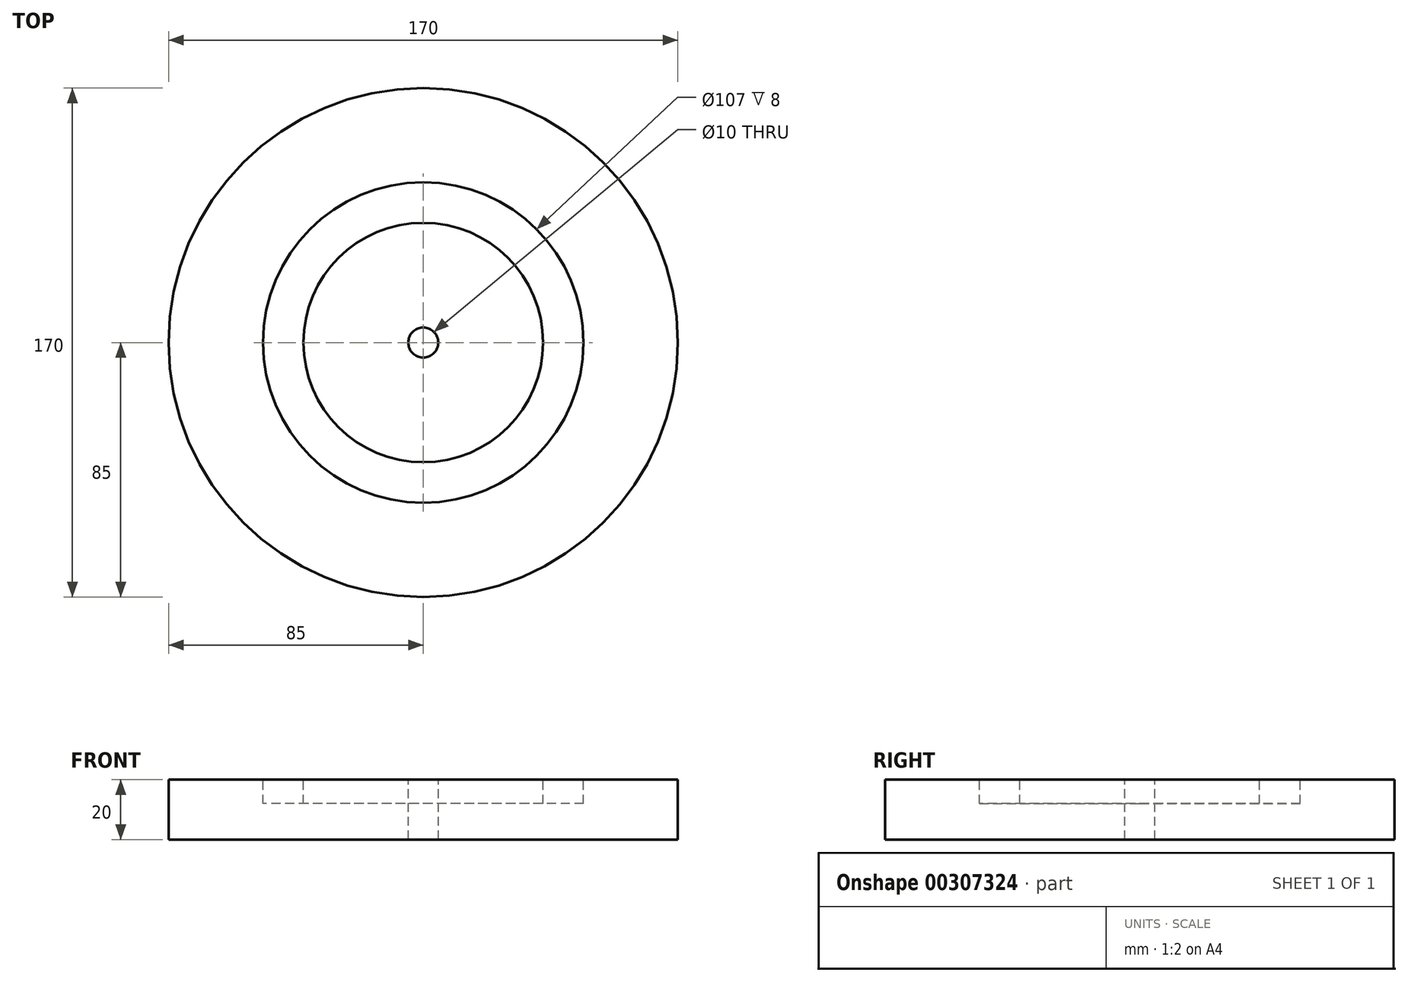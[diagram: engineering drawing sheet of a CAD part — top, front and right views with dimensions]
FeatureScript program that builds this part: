
annotation { "Feature Type Name" : "Feature", "Feature Type Description" : "" }
export const myFeature = defineFeature(function(context is Context, id is Id, definition is map)
    precondition{}
    {
        {
            var Q0;
            Q0=qCreatedBy(makeId("Top.planeOp"),FACE);
            var sketch = newSketch(context, id + "F0", { "sketchPlane" : qUnion([Q0])});
            skCircle(sketch, "E0", {"center": v(0, 0) * mm, "radius": 85 * mm});
            skSolve(sketch);
        }
        {
            var Q0;
            Q0=makeQuery(id+"F0.imprint","IMPRINT",FACE,{"disambiguationData":[TD([[makeQuery(id+"F0.imprint","IMPRINT",EDGE,{"derivedFrom":sQuery(id+"F0.wireOp",EDGE,"E0")}),1.0]])]});
            extrude(context, id + "F1", {"entities" : qUnion([Q0]), "depth" : 20 * mm});
        }
        {
            var Q0;
            Q0=makeQuery(id+"F1.opExtrude","CAP_FACE",FACE,{"disambiguationData":[OSD([sQuery(id+"F0.wireOp",EDGE,"E0")])],"isStart":false});
            var sketch = newSketch(context, id + "F2", { "sketchPlane" : qUnion([Q0])});
            skCircle(sketch, "E1", {"center": v(0, 0) * mm, "radius": 40 * mm});
            skCircle(sketch, "E2", {"center": v(0, 0) * mm, "radius": 53.5 * mm});
            skSolve(sketch);
        }
        {
            var Q0;
            Q0=makeQuery(id+"F2.imprint","IMPRINT",FACE,{"disambiguationData":[TD([[makeQuery(id+"F2.imprint","IMPRINT",EDGE,{"derivedFrom":sQuery(id+"F2.wireOp",EDGE,"E1")}),-1.0]])]});
            extrude(context, id + "F3", {"entities" : qUnion([Q0]), "operationType" : NewBodyOperationType.REMOVE, "oppositeDirection" : true, "depth" : 8 * mm});
        }
        {
            var Q0;
            Q0=makeQuery(id+"F3.boolean.opBoolean","SPLIT",FACE,{"disambiguationData":[TD([makeQuery(id+"F3.opExtrude","SWEPT_FACE",FACE,{"disambiguationData":[OSD([sQuery(id+"F2.wireOp",EDGE,"E1")])]})])],"derivedFrom":makeQuery(id+"F1.opExtrude","CAP_FACE",FACE,{"disambiguationData":[OSD([sQuery(id+"F0.wireOp",EDGE,"E0")])],"isStart":false})});
            var sketch = newSketch(context, id + "F4", { "sketchPlane" : qUnion([Q0])});
            skCircle(sketch, "E3", {"center": v(0, 0) * mm, "radius": 5 * mm});
            skSolve(sketch);
        }
        {
            var Q0;
            Q0 = qSketchRegion(id + "F4", true);
            extrude(context, id + "F5", {"entities" : qUnion([Q0]), "operationType" : NewBodyOperationType.REMOVE, "endBound" : BoundingType.THROUGH_ALL, "oppositeDirection" : true, "depth" : 25.4 * mm});
        }
    });
